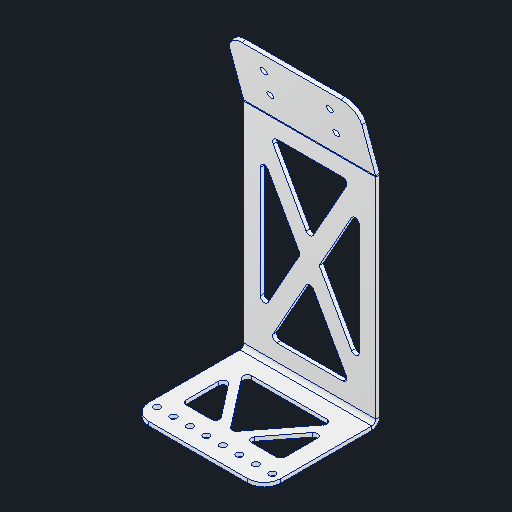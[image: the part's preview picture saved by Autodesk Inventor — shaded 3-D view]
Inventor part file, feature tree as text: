
AUTODESK INVENTOR PART (.ipt)
format: ipt  version: 2024.3 (Build 283343010, 343A)  size: 282,624 bytes
history: native  units: in
note: dims shown in document units (in); Inventor stores cm internally (conversion verified against a paired STEP export)
features: sheet_metal_op x7, sketch x7, other x3, projected_geometry x3, hole x2, extrude x2, chamfer x1
ambient origin geometry x8: Origin, YZ Plane, XZ Plane, XY Plane, X Axis, Y Axis, Z Axis, Center Point
bodies: Solid1 (feature_tree)
feature tree (25):
  sheet_metal_op  "Face1"
  sheet_metal_op  "Flange1"
  hole  "Hole1"  [1 undecoded]
  sheet_metal_op  "Flange2"
  hole  "Hole2"  [1 undecoded]
  extrude  "Extrusion1"  Depth=0.24in
  extrude  "Extrusion2"  Depth=0.12in TaperAngle=15.0deg
  chamfer  "Corner Round2"
  sketch  "Sketch1"  dims[d0=4.0in d1=6.625in]
  other  "Plate1"
  sketch  "Sketch2"  dims[d2=0.12in d3=0.12in]
  other  "Plate2"
  sheet_metal_op  "Bend1"
  sheet_metal_op  "Corner1"
  sketch  "Sketch3"  dims[d4=0.06in d5=0.24in]
  projected_geometry  "Projected Loop1"
  sketch  "Sketch4"  dims[d6=0.12in d7=2.125in d8=15.0deg d9=0.12in]
  other  "Plate3"
  sheet_metal_op  "Bend2"
  sheet_metal_op  "Corner2"
  sketch  "Sketch5"  dims[d10=0.48in]
  projected_geometry  "Projected Loop2"
  sketch  "Sketch6"  dims[d11=0.12in]
  projected_geometry  "Projected Loop3"
  sketch  "Sketch7"  dims[d12=0.12in d13=0.7874in d15=2.0in d16=0.7874in d18=0.75in d21=0.75in d22=0.201in d23=0.75in d24=0.385in d25=0.25in d26=0.5635in d27=0.12in d28=0.8108in d29=0.12in d30=0.06in d31=0.24in d32=0.12in d33=3.5in d34=90.0deg d35=0.12in d36=0.48in d37=0.12in d38=0.12in d39=0.5in d40=0.25in d41=1.5748in d43=0.5in d44=0.3937in d46=1.0in d48=0.201in d49=0.75in d50=0.375in d51=0.25in d52=0.5635in d53=1.0in d54=0.8108in d55=0.5in d56=0.5in d57=0.5in d58=0.125in d59=0.0in d61=0.5in d62=0.5in d63=0.75in d64=0.5in d65=0.5in d66=0.25in d67=0.25in d68=0.0in d69=0.0in d70=0.125in d71=0.125in d72=0.5in]
note: 2 required parameter values undecoded (feature->parameter linkage not recoverable at this tier; creation-order binding heuristic only, values carry confidence <= 0.55)
